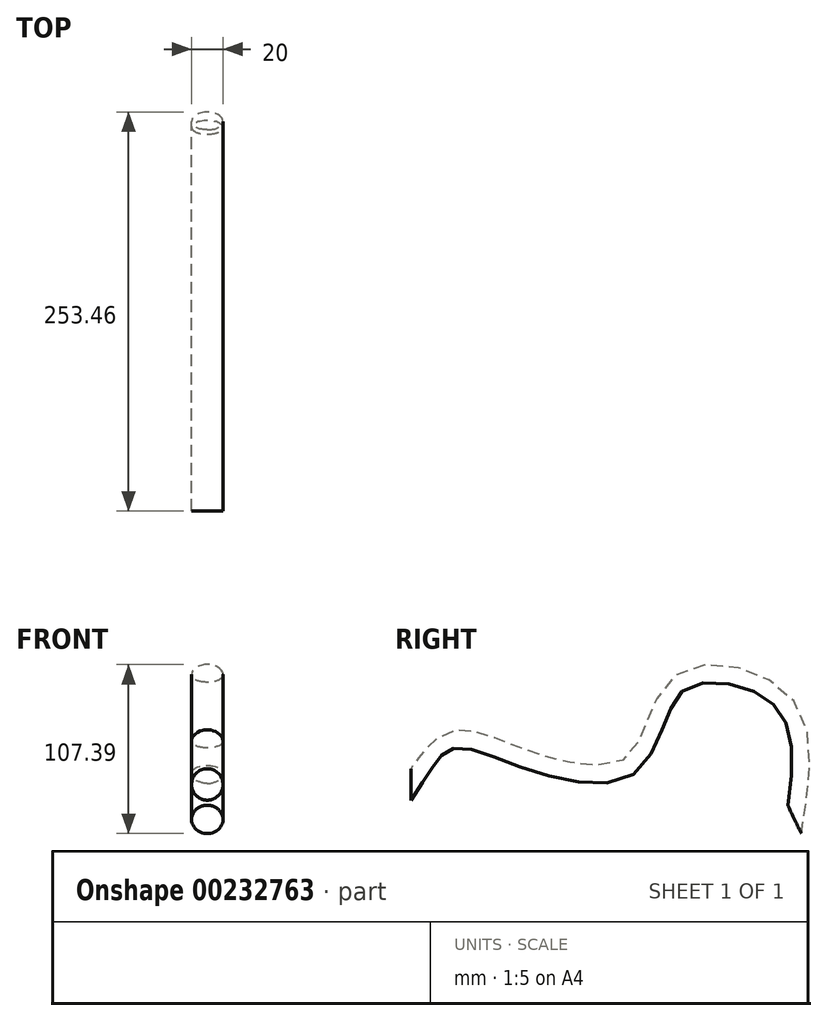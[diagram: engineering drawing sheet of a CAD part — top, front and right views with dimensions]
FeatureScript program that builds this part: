
annotation { "Feature Type Name" : "Feature", "Feature Type Description" : "" }
export const myFeature = defineFeature(function(context is Context, id is Id, definition is map)
    precondition{}
    {
        {
            var Q0;
            Q0=qCreatedBy(makeId("Right.planeOp"),FACE);
            var sketch = newSketch(context, id + "F0", { "sketchPlane" : qUnion([Q0])});
            skFitSpline(sketch, "E0", {"points": [v(0, 0) * mm, v(26.2, 26.89) * mm, v(69.33, 17.33) * mm, v(138.97, 12.96) * mm, v(172.5, 64.5) * mm, v(236.3, 51.4) * mm, v(243.67, -22.2) * mm], "startDerivative": vector(178.74, 264.05) * mm, "endDerivative": vector(-66.13, -444.33) * mm});
            skSolve(sketch);
        }
        {
            var Q0;
            Q0=qCreatedBy(makeId("Front.planeOp"),FACE);
            var sketch = newSketch(context, id + "F1", { "sketchPlane" : qUnion([Q0])});
            skCircle(sketch, "E1", {"center": v(0, 0) * mm, "radius": 10 * mm});
            skSolve(sketch);
        }
        {
            var Q0;
            Q0=makeQuery(id+"F1.imprint","IMPRINT",FACE,{"disambiguationData":[TD([[makeQuery(id+"F1.imprint","IMPRINT",EDGE,{"derivedFrom":sQuery(id+"F1.wireOp",EDGE,"E1")}),1.0]])]});
            var Q1;
            Q1=sQuery(id+"F0.wireOp",EDGE,"E0");
            sweep(context, id + "F2", {"profiles" : qUnion([Q0]), "path" : qUnion([Q1])});
        }
    });
